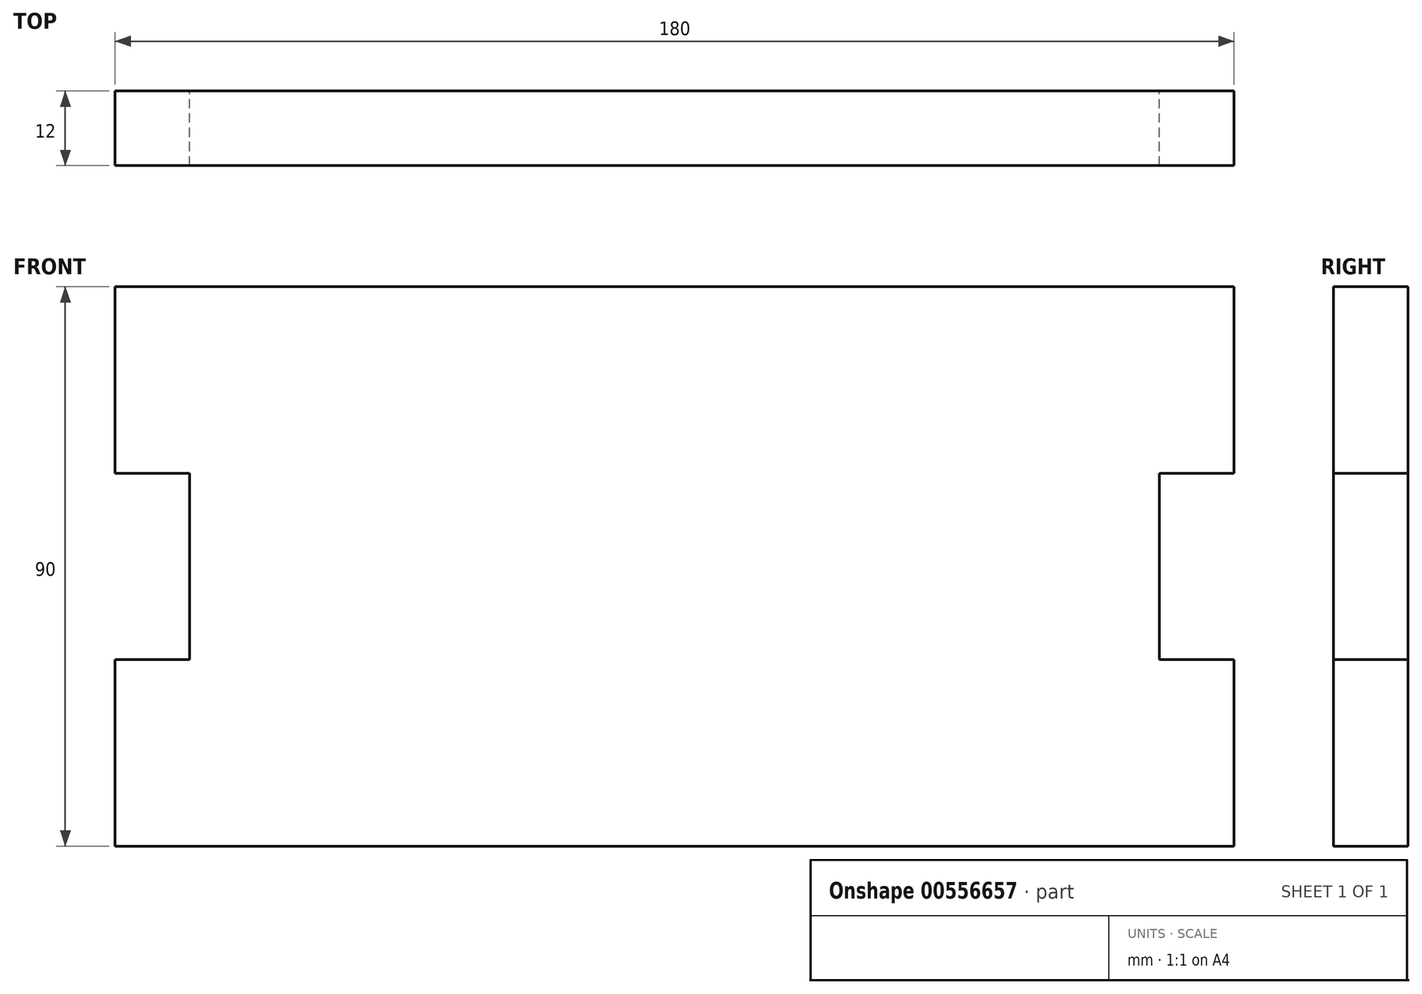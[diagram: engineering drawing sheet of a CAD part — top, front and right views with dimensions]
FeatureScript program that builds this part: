
annotation { "Feature Type Name" : "Feature", "Feature Type Description" : "" }
export const myFeature = defineFeature(function(context is Context, id is Id, definition is map)
    precondition{}
    {
        {
            var Q0;
            Q0=qCreatedBy(makeId("Front.planeOp"),FACE);
            var sketch = newSketch(context, id + "F0", { "sketchPlane" : qUnion([Q0])});
            skLineSegment(sketch, "E0", {"start": v(0, 0) * mm, "end": v(0, 30) * mm});
            skLineSegment(sketch, "E1", {"start": v(0, 30) * mm, "end": v(12, 30) * mm});
            skLineSegment(sketch, "E2", {"start": v(12, 30) * mm, "end": v(12, 60) * mm});
            skLineSegment(sketch, "E3", {"start": v(12, 60) * mm, "end": v(0, 60) * mm});
            skLineSegment(sketch, "E4", {"start": v(0, 60) * mm, "end": v(0, 90) * mm});
            skLineSegment(sketch, "E5", {"start": v(0, 90) * mm, "end": v(90, 90) * mm});
            skLineSegment(sketch, "E6", {"start": v(90, 90) * mm, "end": v(90, 0) * mm, "construction": true});
            skLineSegment(sketch, "E7", {"start": v(90, 0) * mm, "end": v(0, 0) * mm});
            skLineSegment(sketch, "E8.MirrorCS", {"start": v(168, 30) * mm, "end": v(168, 60) * mm});
            skLineSegment(sketch, "E9.MirrorCS", {"start": v(168, 60) * mm, "end": v(180, 60) * mm});
            skLineSegment(sketch, "E10.MirrorCS", {"start": v(90, 0) * mm, "end": v(180, 0) * mm});
            skLineSegment(sketch, "E11.MirrorCS", {"start": v(180, 30) * mm, "end": v(168, 30) * mm});
            skLineSegment(sketch, "E12.MirrorCS", {"start": v(180, 90) * mm, "end": v(90, 90) * mm});
            skLineSegment(sketch, "E13.MirrorCS", {"start": v(180, 60) * mm, "end": v(180, 90) * mm});
            skLineSegment(sketch, "E14.MirrorCS", {"start": v(180, 0) * mm, "end": v(180, 30) * mm});
            skSolve(sketch);
        }
        {
            var Q0;
            Q0 = qSketchRegion(id + "F0", true);
            extrude(context, id + "F1", {"entities" : qUnion([Q0]), "depth" : 12 * mm, "offsetDistance" : 25 * mm});
        }
    });
